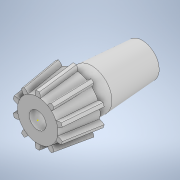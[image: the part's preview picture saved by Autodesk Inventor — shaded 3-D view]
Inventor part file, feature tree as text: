
AUTODESK INVENTOR PART (.ipt)
format: ipt  version: 2021 (Build 250183000, 183)  size: 273,920 bytes
history: native  units: in
note: dims shown in document units (in); Inventor stores cm internally (conversion verified against a paired STEP export)
features: sketch x4, revolve x1, loft x1, pattern_circular x1
ambient origin geometry x8: Origin, YZ Plane, XZ Plane, XY Plane, X Axis, Y Axis, Z Axis, Center Point
bodies: Solid3 (feature_tree)
feature tree (7):
  sketch  "Sketch1"  dims[d20=0.8661in d21=0.3937in]
  revolve  "Revolution2"  [1 undecoded]
  loft  "Loft1"
  pattern_circular  "Circular Pattern1"  Count=3  [1 undecoded]
  sketch  "Sketch5"  dims[d22=0.3937in d23=1.1811in]
  sketch  "Sketch6"  dims[d24=0.9449in]
  sketch  "Sketch7"  dims[d25=0.3937in d26=1.1811in d27=0.9449in d28=0.7874in d29=90.0deg d30=0.1181in d31=0.0591in d32=0.0787in d33=0.0394in d34=0.1969in d35=0.1969in d36=1.1811in d37=0.0591in d38=0.1181in d39=0.7087in d40=0.0394in d41=0.0787in d42=0.1969in d43=0.1969in d44=0.0in d45=90.0deg d46=0.0in d47=90.0deg d48=3.937in d49=360.0deg d7=0.0197in d8=0.0344in d9=0.0197in d10=0.0344in]
note: 2 required parameter values undecoded (feature->parameter linkage not recoverable at this tier; creation-order binding heuristic only, values carry confidence <= 0.55)